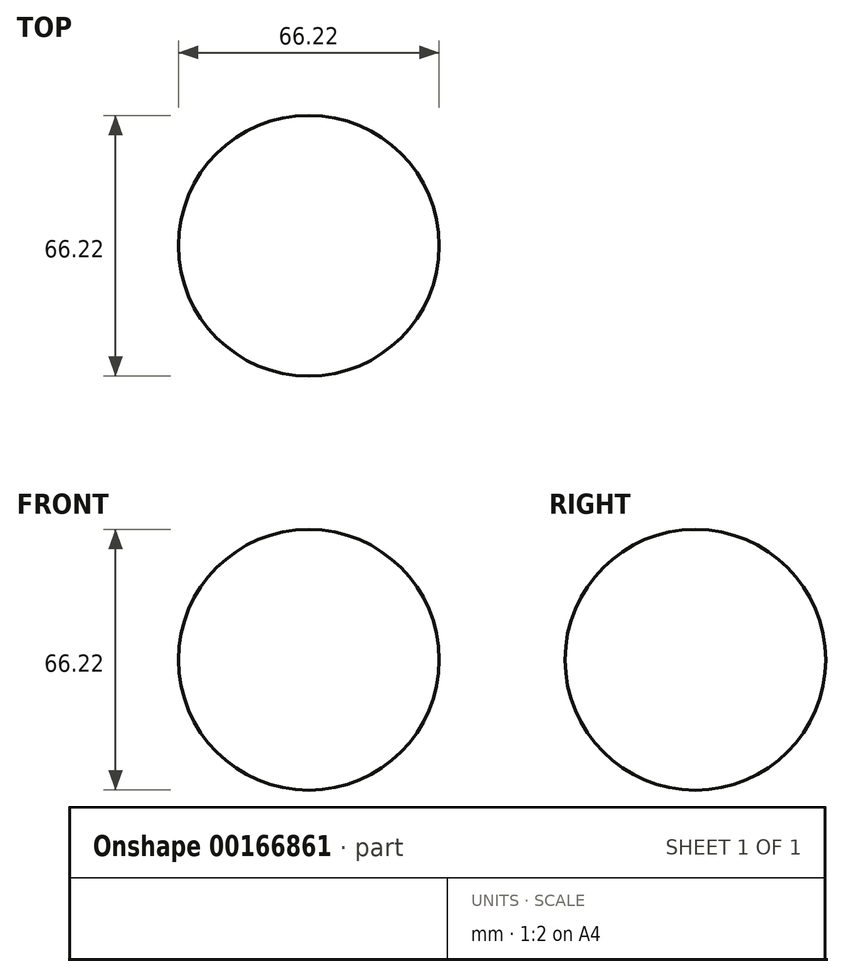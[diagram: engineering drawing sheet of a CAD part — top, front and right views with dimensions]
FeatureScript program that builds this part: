
annotation { "Feature Type Name" : "Feature", "Feature Type Description" : "" }
export const myFeature = defineFeature(function(context is Context, id is Id, definition is map)
    precondition{}
    {
        {
            var Q0;
            Q0=qCreatedBy(makeId("Front.planeOp"),FACE);
            var sketch = newSketch(context, id + "F0", { "sketchPlane" : qUnion([Q0])});
            skArc(sketch, "E0", {"start": v(0, 33.11) * mm, "mid": v(33.11, 0) * mm, "end": v(0, -33.11) * mm});
            skLineSegment(sketch, "E1", {"start": v(0, 33.11) * mm, "end": v(0, -33.11) * mm, "construction": true});
            skSolve(sketch);
        }
        {
            var Q0;
            Q0=sQuery(id+"F0.wireOp",EDGE,"E0");
            var Q1;
            Q1=sQuery(id+"F0.wireOp",EDGE,"E1");
            revolve(context, id + "F1", {"bodyType" : ToolBodyType.SURFACE, "surfaceEntities" : qUnion([Q0]), "axis" : qUnion([Q1]), "revolveType" : RevolveType.FULL});
        }
    });
